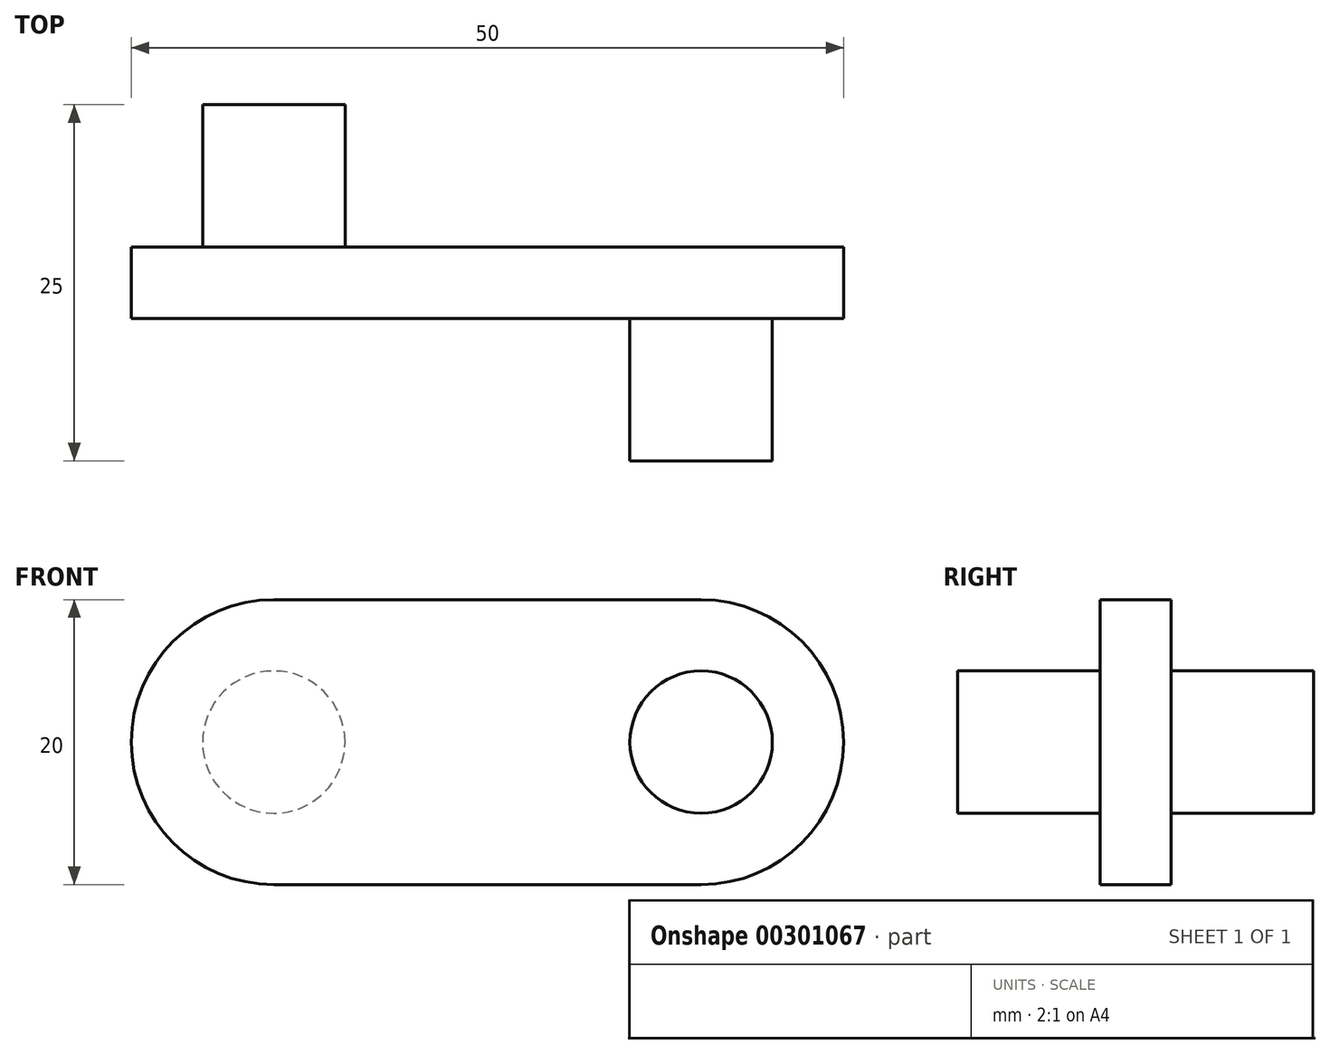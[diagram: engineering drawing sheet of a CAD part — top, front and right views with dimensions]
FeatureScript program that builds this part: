
annotation { "Feature Type Name" : "Feature", "Feature Type Description" : "" }
export const myFeature = defineFeature(function(context is Context, id is Id, definition is map)
    precondition{}
    {
        {
            var Q0;
            Q0=qCreatedBy(makeId("Front.planeOp"),FACE);
            var sketch = newSketch(context, id + "F0", { "sketchPlane" : qUnion([Q0])});
            skArc(sketch, "E0", {"start": v(0, 10) * mm, "mid": v(-10, 0) * mm, "end": v(0, -10) * mm});
            skLineSegment(sketch, "E1", {"start": v(0, 10) * mm, "end": v(30, 10) * mm});
            skLineSegment(sketch, "E2", {"start": v(0, -10) * mm, "end": v(30, -10) * mm});
            skArc(sketch, "E3", {"start": v(30, -10) * mm, "mid": v(40, 0) * mm, "end": v(30, 10) * mm});
            skSolve(sketch);
        }
        {
            var Q0;
            Q0 = qSketchRegion(id + "F0", true);
            extrude(context, id + "F1", {"entities" : qUnion([Q0]), "depth" : 5 * mm});
        }
        {
            var Q0;
            Q0=makeQuery(id+"F1.opExtrude","CAP_FACE",FACE,{"disambiguationData":[OSD([sQuery(id+"F0.wireOp",EDGE,"E0"),sQuery(id+"F0.wireOp",EDGE,"E1"),sQuery(id+"F0.wireOp",EDGE,"E2"),sQuery(id+"F0.wireOp",EDGE,"E3")])],"isStart":false});
            var sketch = newSketch(context, id + "F2", { "sketchPlane" : qUnion([Q0])});
            skCircle(sketch, "E4", {"center": v(30, 0) * mm, "radius": 5 * mm});
            skSolve(sketch);
        }
        {
            var Q0;
            Q0 = qSketchRegion(id + "F2", true);
            extrude(context, id + "F3", {"entities" : qUnion([Q0]), "operationType" : NewBodyOperationType.ADD, "depth" : 10 * mm});
        }
        {
            var Q0;
            Q0=makeQuery(id+"F1.opExtrude","CAP_FACE",FACE,{"disambiguationData":[OSD([sQuery(id+"F0.wireOp",EDGE,"E0"),sQuery(id+"F0.wireOp",EDGE,"E1"),sQuery(id+"F0.wireOp",EDGE,"E2"),sQuery(id+"F0.wireOp",EDGE,"E3")])],"isStart":true});
            var sketch = newSketch(context, id + "F4", { "sketchPlane" : qUnion([Q0])});
            skCircle(sketch, "E5", {"center": v(0, 0) * mm, "radius": 5 * mm});
            skSolve(sketch);
        }
        {
            var Q0;
            Q0 = qSketchRegion(id + "F4", true);
            extrude(context, id + "F5", {"entities" : qUnion([Q0]), "operationType" : NewBodyOperationType.ADD, "depth" : 10 * mm});
        }
    });
